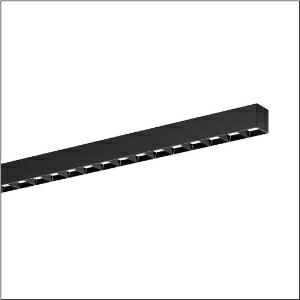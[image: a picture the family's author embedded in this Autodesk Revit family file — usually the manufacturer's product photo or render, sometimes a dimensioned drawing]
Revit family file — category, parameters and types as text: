
# Revit family: silica_r__21_51mx24tctab_feaf
name_source: partatom
category: Lighting Fixtures
units: mm (PartAtom-declared; Revit-internal decimal feet)

## family parameters
Cut with Voids When Loaded = No
Host = Face
Light Source = No
Part Type = Normal
Room Calculation Point = No
Round Connector Dimension = Use Diameter
Shared = No

## types (1)
- --- (1 x LED, 8200 lm, 81.1 W, 6500K)
    Apparent Load = 81 VA
    CIE Flux Codes = 74 94 99 100 100
    Color Rendering = 80
    Color Temperature = 6500K
    Default Elevation = 1800 mm
    Description = Silica® 21, office luminaire, primary light control with darklight reflector, of PMMA, black, light emission: direct distribution, primary light characteristic: asymmetric, installation type: surface-mounted, LED, rated luminous flux: 8.200lm, luminous efficacy: 96lm/W, light colour: 8tw, colour temperature: 2700..6500K, control gear: ECG DALI, with terminal, 3+2-pole, max. 2.5mm², mains connection: 220..240V, AC, 50/60Hz, rated input power: 85.2W, luminaire housing, of aluminium, jet black (RAL 9005), length: 3.004mm, width: 53mm, height: 53mm, protection rating (complete): IP20, insulation class (complete): insulation class I (protective earthing), certification: CE, permissible operating ambient temperature: 0..+35°C, standard: EN 50419, packaging unit: 1 piece
    Height = 0 mm  [stored 0 ft]
    Lamp = 1 x LED
    Lamp Light Flux = 8200 lm
    Lamp Power = 81.1 W
    Lamp count = 1
    Length = 3004 mm
    Luminous efficacy = 101 lm/W
    Manufacturer = Siteco
    ModVariant = No
    Model = 51MX24TCTAB
    Mounting Place = Ceiling
    Mounting Type = Recessed
    Number of Poles = 1
    OnlyDefault = Yes
    Power Factor = 1
    Product Name = Silica® 21
    Product group = office luminaire | ceiling recessed
    ProductGroupID = 400
    Protection Class = Protection class I
    Protection Degree = IP 20
    RLX_Detail_Level = 1
    RLX_Emergency_Light_Flux = 0 lm
    RLX_Emergency_Type = 0
    RLX_Emergency_Type_DB = No
    RlxData = <blob elided: 61049 chars, md5=1cc460ce>
    Socket = socket
    Standby Power = 0 W
    System Light Flux = 8200 lm
    System Power = 81 W
    Type Comments = individual setting
    Type Image = l_1335908.jpg
    URL = http://relux.com
    VarID = @adj_109789
    Voltage = 0 V
    Weight = 0.00 kg
    Width = 53 mm

note: [stored X ft] marks values corroborated as IEEE doubles in the binary element streams (Revit-internal decimal feet)

## geometry (parser evidence)
native form markers: Blend x4, Sweep x12
no freeform markers — native parametric forms only
